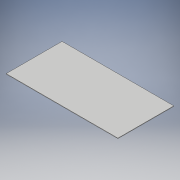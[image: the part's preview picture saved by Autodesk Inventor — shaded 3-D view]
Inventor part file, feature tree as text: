
AUTODESK INVENTOR PART (.ipt)
format: ipt  version: 2018 (Build 220112000, 112)  size: 89,088 bytes
history: native  units: in
note: dims shown in document units (in); Inventor stores cm internally (conversion verified against a paired STEP export)
features: extrude x1, sketch x1
ambient origin geometry x8: Origin, YZ Plane, XZ Plane, XY Plane, X Axis, Y Axis, Z Axis, Center Point
bodies: Solid1 (feature_tree)
feature tree (2):
  extrude  "Extrusion1"  Depth=120.0in
  sketch  "Sketch1"  dims[d0=240.0in d1=120.0in d2=1.0in d3=0.0in]
